# Revit family: Сборная площадка 1.151.1-8.1
name_source: partatom
category: Каркас несущий
revit_build: Autodesk Revit Structure 2016 (Build: 20150220_1215(x64)
units: mm (PartAtom-declared; Revit-internal decimal feet)

## family parameters
Всегда вертикально = Да
Всегда экспортировать в виде геометрии = Нет
Материал для поведения модели = Прочее
На основе рабочей плоскости = Нет
Общий = Нет
Округление длины несущего каркаса = 0 мм
Показывать семейство разрезанным на планах = Да
При загрузке вырезать с полостями = Нет
Условное обозначение = Из семейства
Форма сечения = Не задано

## types (2) — shared parameters
Длина L = 2500 мм

## per-type parameters (varying)
| type | Изготовитель | Масса | Ширина B |
| 2ЛП 25-12-4-к | серия 1.152.1-8.1 3000 | 1160 | 1300 мм |
| 2ЛП 25-15-4-к | серия 1.152.1-8.1 3000-01 | 1345 | 1600 мм |

note: column(s) folded — value = type name in every type: Описание

## geometry (parser evidence)
native form markers: Blend x8
no freeform markers — native parametric forms only
